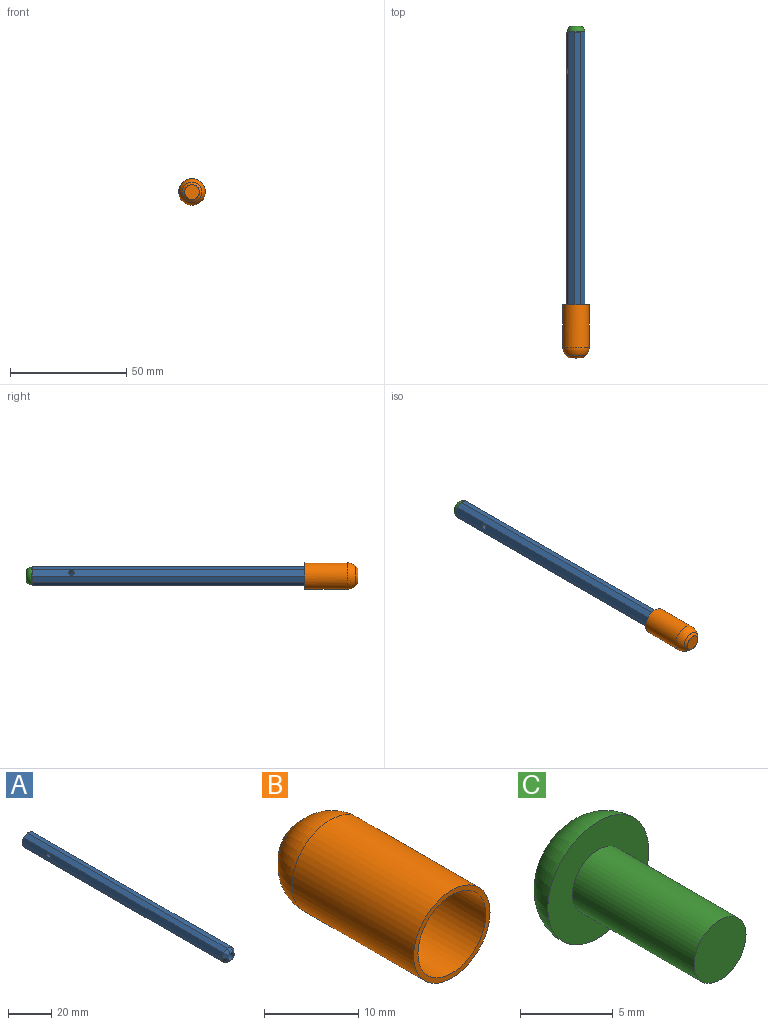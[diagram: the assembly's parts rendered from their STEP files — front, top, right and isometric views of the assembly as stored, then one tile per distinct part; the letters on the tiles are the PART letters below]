
ASSEMBLY  parts=3 mates=2
PART A: 21 faces, bbox 7.9x132.9x8.1 mm
  f0: plane 130.91x2.15mm, normal (0.77,0,-0.64), area 366.7mm2, adj f1,f9,f10,f17
  f1: plane 130.91x2.8mm, normal (1,0,0), area 366.7mm2, adj f0,f2,f10,f19
  f2: plane 130.91x2.15mm, normal (0.77,0,0.64), area 366.7mm2, adj f1,f3,f10,f18
  f3: plane 130.91x2.76mm, normal (0.17,0,0.98), area 366.7mm2, adj f2,f4,f10,f16
  f4: plane 130.91x2.43mm, normal (-0.5,0,0.87), area 366.7mm2, adj f3,f5,f10,f14
  f5: plane 130.91x2.63mm, normal (-0.94,0,0.34), area 362.6mm2, adj f4,f6,f10,f12,f20
  f6: plane 130.91x2.63mm, normal (-0.94,0,-0.34), area 366.7mm2, adj f5,f7,f10,f11
  f7: plane 130.91x2.43mm, normal (-0.5,0,-0.87), area 366.7mm2, adj f6,f9,f10,f13
  f8: cylinder r=2.02mm len=132.86mm, axis (0,1,0), area 1680.4mm2, adj f10,f11,f12,f13,f14,f15,f16,f17
  f9: plane 130.91x2.76mm, normal (0.17,0,-0.98), area 366.7mm2, adj f0,f7,f10,f15
  f10: plane 8.07x7.94mm, normal (0,1,0), area 35.7mm2, adj f0,f1,f2,f3,f4,f5,f6,f7
  f11: plane 2.63x2.55mm, normal (-0.66,-0.71,-0.24), area 5.6mm2, adj f6,f8,f12,f13
  f12: plane 2.63x2.55mm, normal (-0.66,-0.71,0.24), area 5.6mm2, adj f5,f8,f11,f14
  f13: plane 2.79x2.74mm, normal (-0.35,-0.71,-0.61), area 5.6mm2, adj f7,f8,f11,f15
  f14: plane 2.79x2.74mm, normal (-0.35,-0.71,0.61), area 5.6mm2, adj f4,f8,f12,f16
  f15: plane 2.76x2.28mm, normal (0.12,-0.71,-0.7), area 5.6mm2, adj f8,f9,f13,f17
  f16: plane 2.76x2.28mm, normal (0.12,-0.71,0.7), area 5.6mm2, adj f3,f8,f14,f18
  f17: plane 2.86x2.84mm, normal (0.54,-0.71,-0.45), area 5.6mm2, adj f0,f8,f15,f19
  f18: plane 2.86x2.84mm, normal (0.54,-0.71,0.45), area 5.6mm2, adj f2,f8,f16,f19
  f19: plane 2.8x1.95mm, normal (0.71,-0.71,0), area 5.6mm2, adj f1,f8,f17,f18
  f20: cylinder r=1.14mm len=2.9mm, axis (-0.94,0,0.34), area 14.4mm2, adj f5,f8
PART B: 7 faces, bbox 11.4x22.9x11.4 mm
  f0: cylinder r=5.71mm len=18.22mm, axis (0,1,0), area 654.1mm2, adj f1,f6
  f1: plane 11.43x11.43mm, normal (0,-1,0), area 21.5mm2, adj f0,f3
  f2: plane 6.35x6.35mm, normal (0,1,0), area 31.7mm2, adj f5
  f3: cylinder r=5.08mm len=17.78mm, axis (0,-1,0), area 567.5mm2, adj f1,f4
  f4: plane 10.16x10.16mm, normal (0,-1,0), area 81.1mm2, adj f3
  f5: cone r=5.71mm half-angle=45deg, axis (0,-1,0), area 34.6mm2, adj f2,f6
  f6: torus R=0.64mm, axis (0,1,0), area 130.6mm2, adj f0,f5
PART C: 5 faces, bbox 7.7x11.8x7.7 mm
  f0: cylinder r=1.98mm len=9.27mm, axis (0,1,0), area 115.4mm2, adj f1,f3
  f1: plane 3.96x3.96mm, normal (0,-1,0), area 12.3mm2, adj f0
  f2: plane 2.62x2.62mm, normal (0,1,0), area 5.4mm2, adj f4
  f3: plane 7.7x7.7mm, normal (0,-1,0), area 34.2mm2, adj f0,f4
  f4: torus R=1.31mm, axis (0,1,0), area 73.3mm2, adj f2,f3
PLACE A t=(-20.2,27.21,31.13)mm
PLACE B rot(axis=(1,0,0),180deg) t=(-20.2,-112.98,31.13)mm
PLACE C t=(-20.2,27.27,31.13)mm
MATE slider C.f0 <-> A.f8  axis (0,-1,0) through (-20.2,18,31.13)mm
MATE slider B.f3 <-> A.f8  axis (0,1,0) through (-20.2,-90.12,31.13)mm
